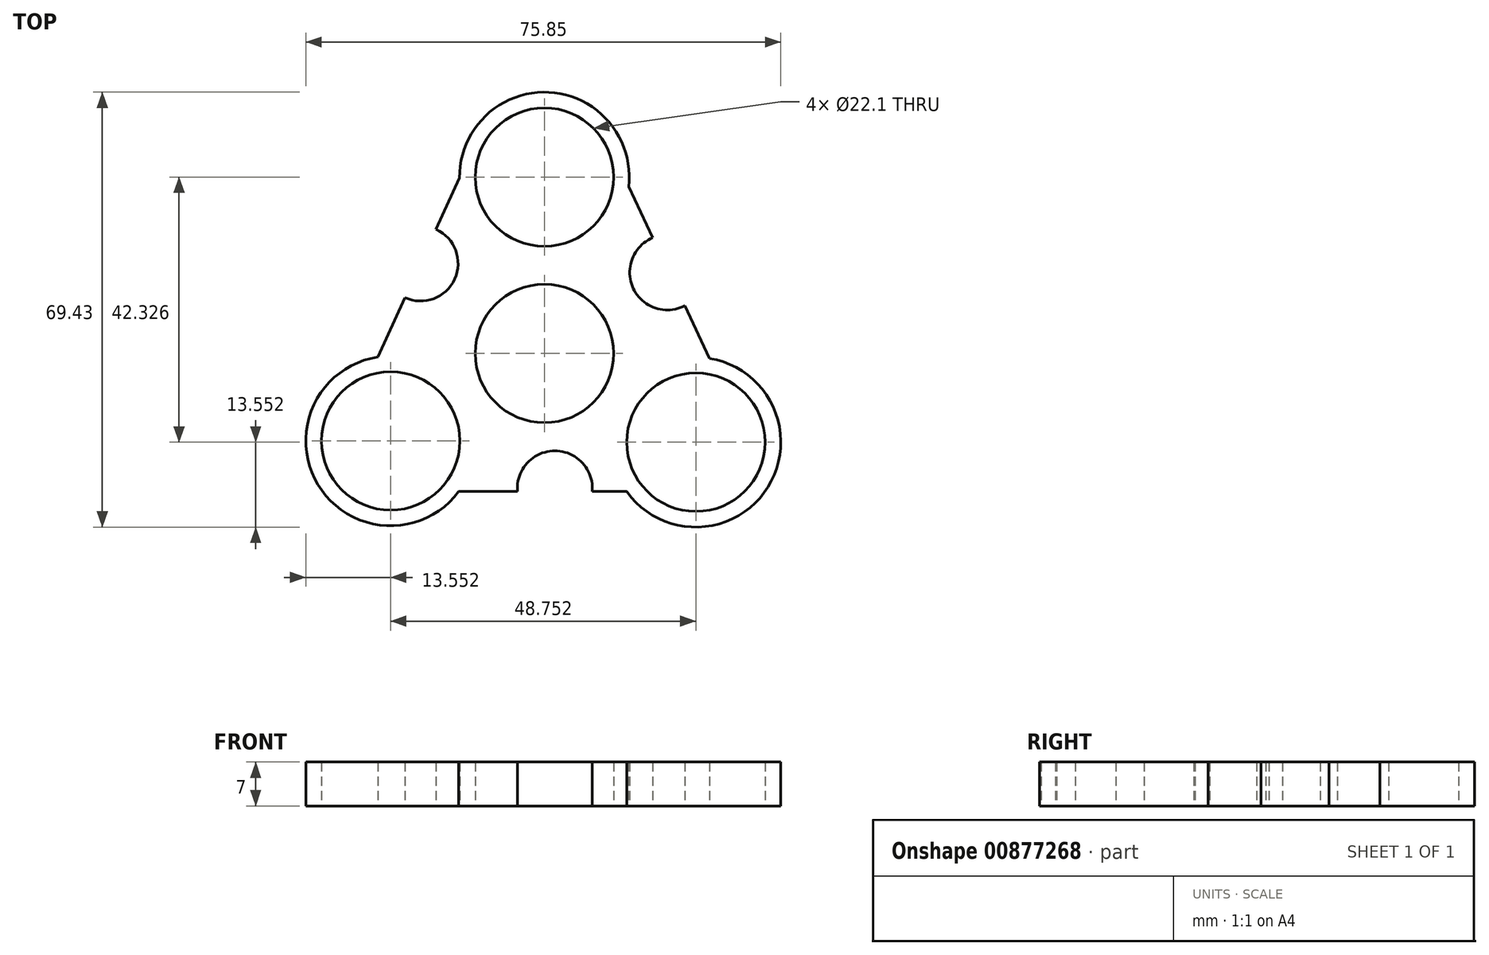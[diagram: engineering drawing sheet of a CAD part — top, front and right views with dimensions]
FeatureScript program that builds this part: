
annotation { "Feature Type Name" : "Feature", "Feature Type Description" : "" }
export const myFeature = defineFeature(function(context is Context, id is Id, definition is map)
    precondition{}
    {
        {
            var Q0;
            Q0=qCreatedBy(makeId("Top.planeOp"),FACE);
            var sketch = newSketch(context, id + "F0", { "sketchPlane" : qUnion([Q0])});
            skCircle(sketch, "E0", {"center": v(0, 0) * mm, "radius": 11.05 * mm});
            skCircle(sketch, "E1", {"center": v(0, 0) * mm, "radius": 13.55 * mm});
            skCircle(sketch, "E2", {"center": v(0, 28.16) * mm, "radius": 11.05 * mm});
            skCircle(sketch, "E3", {"center": v(0, 28.16) * mm, "radius": 13.55 * mm});
            skCircle(sketch, "E4.1.0", {"center": v(-24.56, -13.96) * mm, "radius": 11.05 * mm});
            skCircle(sketch, "E4.1.1", {"center": v(-24.56, -13.96) * mm, "radius": 13.55 * mm});
            skCircle(sketch, "E4.2.0", {"center": v(24.2, -14.17) * mm, "radius": 11.05 * mm});
            skCircle(sketch, "E4.2.1", {"center": v(24.2, -14.17) * mm, "radius": 13.55 * mm});
            skPoint(sketch, "E4.center", {"position": v(-0.12, 0.01) * mm});
            skLineSegment(sketch, "E5", {"start": v(-13.69, -22.04) * mm, "end": v(-4.31, -22.04) * mm});
            skLineSegment(sketch, "E6", {"start": v(13.46, 26.6) * mm, "end": v(17.29, 18.47) * mm});
            skArc(sketch, "E7", {"start": v(17.29, 18.47) * mm, "mid": v(14.2, 10.39) * mm, "end": v(22.4, 7.63) * mm});
            skArc(sketch, "E8", {"start": v(7.65, -22.04) * mm, "mid": v(1.67, -15.54) * mm, "end": v(-4.31, -22.04) * mm});
            skLineSegment(sketch, "E9.trimOffspring", {"start": v(22.4, 7.63) * mm, "end": v(26.37, -0.8) * mm});
            skLineSegment(sketch, "E10.trimOffspring", {"start": v(7.65, -22.04) * mm, "end": v(13.17, -22.04) * mm});
            skLineSegment(sketch, "E11", {"start": v(-13.55, 28.01) * mm, "end": v(-17.3, 19.83) * mm});
            skArc(sketch, "E12", {"start": v(-22.28, 8.91) * mm, "mid": v(-14.33, 11.87) * mm, "end": v(-17.3, 19.83) * mm});
            skLineSegment(sketch, "E13.trimOffspring", {"start": v(-22.28, 8.91) * mm, "end": v(-26.61, -0.56) * mm});
            skSolve(sketch);
        }
        {
            var Q0;
            Q0=makeQuery(id+"F0.imprint","IMPRINT",FACE,{"disambiguationData":[TD([[makeQuery(id+"F0.imprint","IMPRINT",EDGE,{"derivedFrom":sQuery(id+"F0.wireOp",EDGE,"E1")}),-1.0]])]});
            var Q1;
            Q1=makeQuery(id+"F0.imprint","IMPRINT",FACE,{"disambiguationData":[TD([[makeQuery(id+"F0.imprint","IMPRINT",EDGE,{"derivedFrom":sQuery(id+"F0.wireOp",EDGE,"E4.2.0")}),-1.0]])]});
            var Q2;
            Q2=makeQuery(id+"F0.imprint","IMPRINT",FACE,{"disambiguationData":[TD([[makeQuery(id+"F0.imprint","IMPRINT",EDGE,{"derivedFrom":sQuery(id+"F0.wireOp",EDGE,"E4.1.0")}),-1.0]])]});
            var Q3;
            Q3=makeQuery(id+"F0.imprint","IMPRINT",FACE,{"disambiguationData":[TD([[makeQuery(id+"F0.imprint","IMPRINT",EDGE,{"derivedFrom":sQuery(id+"F0.wireOp",EDGE,"E0")}),-1.0]])]});
            var Q4;
            Q4=makeQuery(id+"F0.imprint","IMPRINT",FACE,{"disambiguationData":[TD([[makeQuery(id+"F0.imprint","IMPRINT",EDGE,{"derivedFrom":sQuery(id+"F0.wireOp",EDGE,"E2")}),-1.0]])]});
            extrude(context, id + "F1", {"entities" : qUnion([Q0, Q1, Q2, Q3, Q4]), "depth" : 7 * mm, "offsetDistance" : 25 * mm});
        }
    });
